# Revit family: 放水型SP現地操作盤埋込
name_source: partatom
category: 機械設備
revit_build: Autodesk Revit 2018 (Build: 20170223_1515(x64)
units: mm (PartAtom-declared; Revit-internal decimal feet)

## family parameters
OmniClass タイトル = Fire Fighting Terminal Components
OmniClass 番号 = 23.65.70.17.11
パーツ タイプ = 標準
ロード時にボイドで切り取り = いいえ
丸型コネクタ寸法 = 直径を使用
作業面ベース = いいえ
共有 = いいえ
常に垂直 = はい
種別 = なし
部屋計算ポイント = いいえ

## types (1)
- 放水型SP制御盤埋込型
    Depth = 200
    Height = 350  [stored 1.14829 ft]
    IfcExportAs = IfcFireSuppressionTerminalType
    IfcExportType = Sprinkler
    OmniClassCode = 23-65 70 17 11
    URL = https://www.yamatoprotec.co.jp
    Uniclass2015Code = Pr_75_50_33_28
    Uniclass2015Title = Extinguishing control panels
    Uniclass2015Version = Systems v1.9
    Width = 550
    アセンブリ コード = D4030900
    キーノート = 283100
    仕様書バージョン = Version1.0
    企業コード = 580077214
    分類コード = 50903008000020
    呼称 = 放水型SP制御盤埋込型
    形式 = 屋内型
    形式2 = 埋込型
    積算_科目 = 9 消火設備
    製造元 = ヤマトプロテック株式会社
    質量 = 0.00 kg

note: [stored X ft] marks values corroborated as IEEE doubles in the binary element streams (Revit-internal decimal feet)
